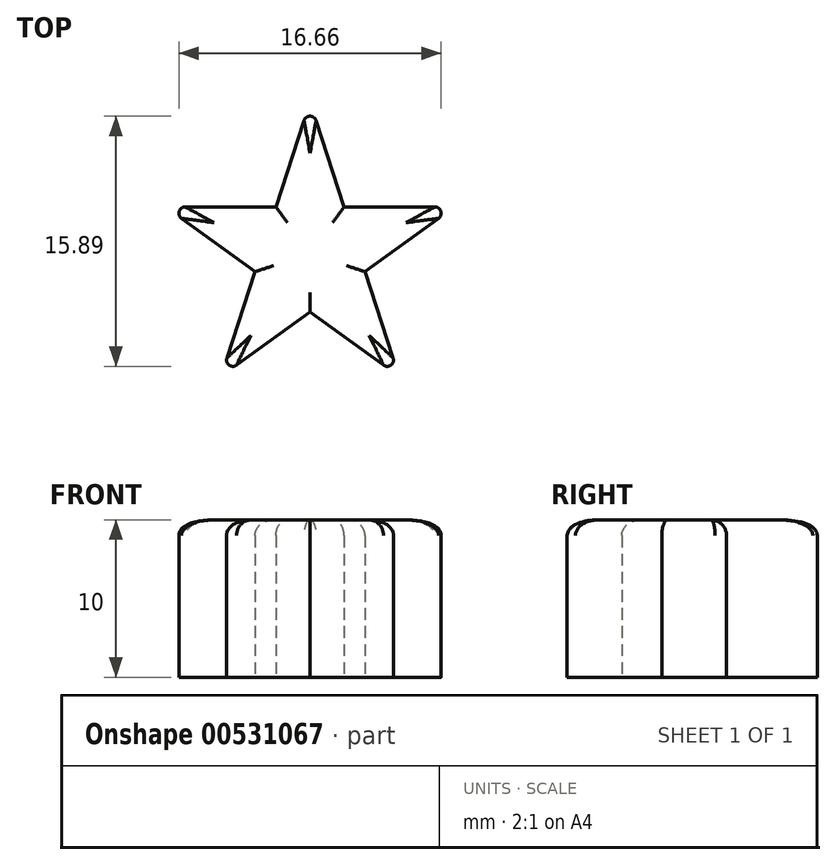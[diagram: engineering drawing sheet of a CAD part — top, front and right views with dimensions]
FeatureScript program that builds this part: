
annotation { "Feature Type Name" : "Feature", "Feature Type Description" : "" }
export const myFeature = defineFeature(function(context is Context, id is Id, definition is map)
    precondition{}
    {
        {
            var Q0;
            Q0=qCreatedBy(makeId("Top.planeOp"),FACE);
            var sketch = newSketch(context, id + "F0", { "sketchPlane" : qUnion([Q0])});
            skLineSegment(sketch, "E0", {"start": v(0, 35.92) * mm, "end": v(0, -40.46) * mm, "construction": true});
            skLineSegment(sketch, "E1", {"start": v(-0.38, 34.75) * mm, "end": v(-2.16, 29.27) * mm});
            skLineSegment(sketch, "E2", {"start": v(-2.16, 29.27) * mm, "end": v(-7.93, 29.27) * mm});
            skLineSegment(sketch, "E3", {"start": v(-8.17, 28.54) * mm, "end": v(-3.5, 25.15) * mm});
            skLineSegment(sketch, "E4", {"start": v(-3.5, 25.15) * mm, "end": v(-5.28, 19.66) * mm});
            skLineSegment(sketch, "E5", {"start": v(-4.67, 19.22) * mm, "end": v(0, 22.6) * mm});
            skLineSegment(sketch, "E6.MirrorCS", {"start": v(0.38, 34.75) * mm, "end": v(2.16, 29.27) * mm});
            skLineSegment(sketch, "E7.MirrorCS", {"start": v(2.16, 29.27) * mm, "end": v(7.93, 29.27) * mm});
            skLineSegment(sketch, "E8.MirrorCS", {"start": v(8.17, 28.54) * mm, "end": v(3.5, 25.15) * mm});
            skLineSegment(sketch, "E9.MirrorCS", {"start": v(3.5, 25.15) * mm, "end": v(5.28, 19.66) * mm});
            skLineSegment(sketch, "E10.MirrorCS", {"start": v(4.67, 19.22) * mm, "end": v(0, 22.6) * mm});
            skPoint(sketch, "E11.visualSharp", {"position": v(0, 35.92) * mm});
            skArc(sketch, "E11.filletArc", {"start": v(0.38, 34.75) * mm, "mid": v(0, 35.03) * mm, "end": v(-0.38, 34.75) * mm});
            skPoint(sketch, "E12.visualSharp", {"position": v(-9.16, 29.27) * mm});
            skArc(sketch, "E12.filletArc", {"start": v(-7.93, 29.27) * mm, "mid": v(-8.31, 28.99) * mm, "end": v(-8.17, 28.54) * mm});
            skPoint(sketch, "E13.visualSharp", {"position": v(9.16, 29.27) * mm});
            skArc(sketch, "E13.filletArc", {"start": v(8.17, 28.54) * mm, "mid": v(8.31, 28.99) * mm, "end": v(7.93, 29.27) * mm});
            skPoint(sketch, "E14.visualSharp", {"position": v(-5.66, 18.5) * mm});
            skArc(sketch, "E14.filletArc", {"start": v(-5.28, 19.66) * mm, "mid": v(-5.14, 19.22) * mm, "end": v(-4.67, 19.22) * mm});
            skPoint(sketch, "E15.visualSharp", {"position": v(5.66, 18.5) * mm});
            skArc(sketch, "E15.filletArc", {"start": v(4.67, 19.22) * mm, "mid": v(5.14, 19.22) * mm, "end": v(5.28, 19.66) * mm});
            skSolve(sketch);
        }
        {
            var Q0;
            Q0=makeQuery(id+"F0.imprint","IMPRINT",FACE,{"disambiguationData":[TD([[makeQuery(id+"F0.imprint","IMPRINT",EDGE,{"derivedFrom":sQuery(id+"F0.wireOp",EDGE,"E1")}),1.0]])]});
            extrude(context, id + "F1", {"entities" : qUnion([Q0]), "depth" : 10 * mm, "offsetDistance" : 25 * mm});
        }
        {
            var Q0;
            Q0=makeQuery(id+"F1.opExtrude","CAP_FACE",FACE,{"disambiguationData":[OSD([sQuery(id+"F0.wireOp",EDGE,"E1"),sQuery(id+"F0.wireOp",EDGE,"E2"),sQuery(id+"F0.wireOp",EDGE,"E3"),sQuery(id+"F0.wireOp",EDGE,"E4"),sQuery(id+"F0.wireOp",EDGE,"E5"),sQuery(id+"F0.wireOp",EDGE,"E6.MirrorCS"),sQuery(id+"F0.wireOp",EDGE,"E7.MirrorCS"),sQuery(id+"F0.wireOp",EDGE,"E8.MirrorCS"),sQuery(id+"F0.wireOp",EDGE,"E9.MirrorCS"),sQuery(id+"F0.wireOp",EDGE,"E10.MirrorCS"),sQuery(id+"F0.wireOp",EDGE,"E11.filletArc"),sQuery(id+"F0.wireOp",EDGE,"E12.filletArc"),sQuery(id+"F0.wireOp",EDGE,"E13.filletArc"),sQuery(id+"F0.wireOp",EDGE,"E14.filletArc"),sQuery(id+"F0.wireOp",EDGE,"E15.filletArc")])],"isStart":false});
            fillet(context, id + "F2", {"entities" : qUnion([Q0]), "radius" : 1 * mm, "tangentPropagation" : true, "allowEdgeOverflow" : false});
        }
    });
